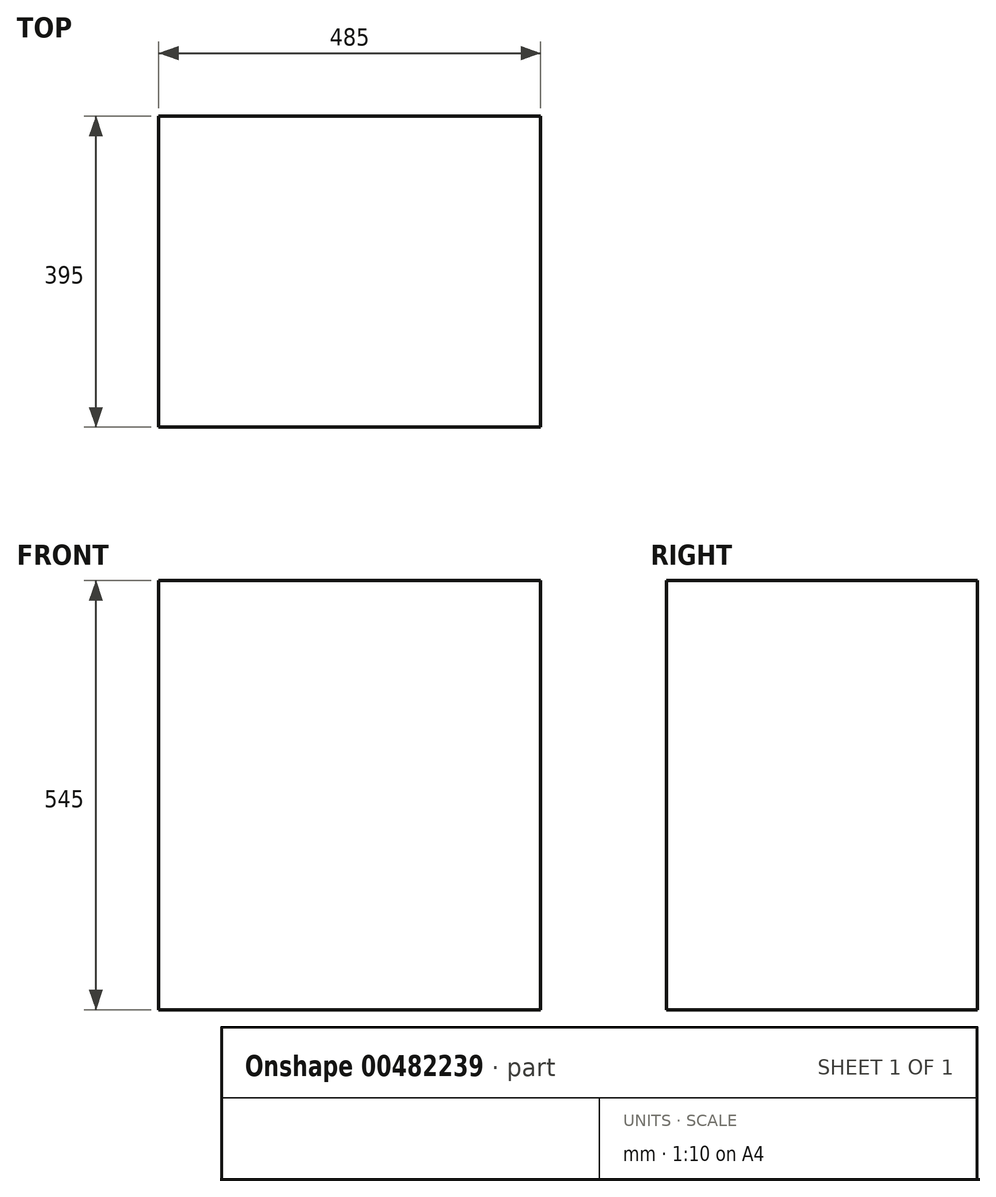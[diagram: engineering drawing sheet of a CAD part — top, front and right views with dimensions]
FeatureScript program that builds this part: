
annotation { "Feature Type Name" : "Feature", "Feature Type Description" : "" }
export const myFeature = defineFeature(function(context is Context, id is Id, definition is map)
    precondition{}
    {
        {
            var Q0;
            Q0=qCreatedBy(makeId("Front.planeOp"),FACE);
            var sketch = newSketch(context, id + "F0", { "sketchPlane" : qUnion([Q0])});
            skLineSegment(sketch, "E0.bottom", {"start": v(-242.5, 272.5) * mm, "end": v(242.5, 272.5) * mm});
            skLineSegment(sketch, "E0.top", {"start": v(-242.5, -272.5) * mm, "end": v(242.5, -272.5) * mm});
            skLineSegment(sketch, "E0.left", {"start": v(-242.5, 272.5) * mm, "end": v(-242.5, -272.5) * mm});
            skLineSegment(sketch, "E0.right", {"start": v(242.5, 272.5) * mm, "end": v(242.5, -272.5) * mm});
            skPoint(sketch, "E0.middle", {"position": v(0, 0) * mm});
            skSolve(sketch);
        }
        {
            var Q0;
            Q0 = qSketchRegion(id + "F0", true);
            extrude(context, id + "F1", {"entities" : qUnion([Q0]), "depth" : 395 * mm});
        }
    });
